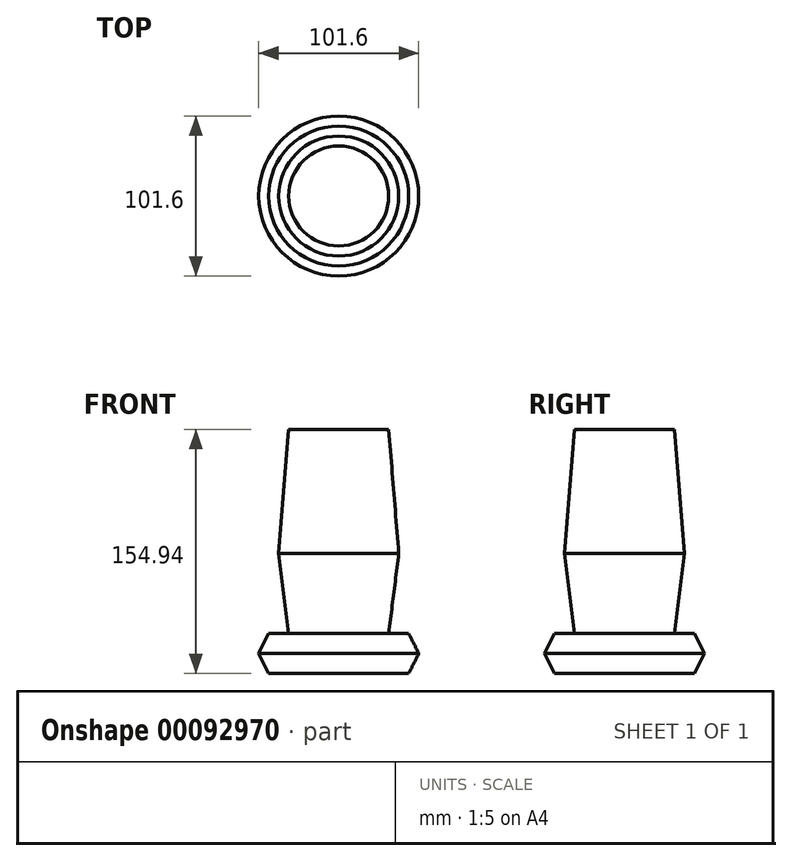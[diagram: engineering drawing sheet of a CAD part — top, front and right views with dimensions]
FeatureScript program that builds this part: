
annotation { "Feature Type Name" : "Feature", "Feature Type Description" : "" }
export const myFeature = defineFeature(function(context is Context, id is Id, definition is map)
    precondition{}
    {
        {
            var Q0;
            Q0=qCreatedBy(makeId("Top.planeOp"),FACE);
            var sketch = newSketch(context, id + "F0", { "sketchPlane" : qUnion([Q0])});
            skCircle(sketch, "E0", {"center": v(0, 0) * mm, "radius": 44.45 * mm});
            skSolve(sketch);
        }
        {
            var Q0;
            Q0=qCreatedBy(makeId("Top.planeOp"),FACE);
            cPlane(context, id + "F1", {"entities" : qUnion([Q0]), "cplaneType" : CPlaneType.OFFSET, "offset" : 12.7 * mm, "width" : 152.4 * mm, "height" : 152.4 * mm});
        }
        {
            var Q0;
            Q0=qCreatedBy(id+"F1.planeOp",FACE);
            var sketch = newSketch(context, id + "F2", { "sketchPlane" : qUnion([Q0])});
            skCircle(sketch, "E1", {"center": v(0, 0) * mm, "radius": 50.8 * mm});
            skSolve(sketch);
        }
        {
            var Q0;
            Q0=makeQuery(id+"F0.imprint","IMPRINT",FACE,{"disambiguationData":[TD([[makeQuery(id+"F0.imprint","IMPRINT",EDGE,{"derivedFrom":sQuery(id+"F0.wireOp",EDGE,"E0")}),1.0]])]});
            var Q1;
            Q1=makeQuery(id+"F2.imprint","IMPRINT",FACE,{"disambiguationData":[TD([[makeQuery(id+"F2.imprint","IMPRINT",EDGE,{"derivedFrom":sQuery(id+"F2.wireOp",EDGE,"E1")}),1.0]])]});
            loft(context, id + "F3", {"sheetProfilesArray" : [{ "sheetProfileEntities" : qUnion([Q0]) }, { "sheetProfileEntities" : qUnion([Q1]) }]});
        }
        {
            var Q0;
            Q0=qCreatedBy(id+"F1.planeOp",FACE);
            cPlane(context, id + "F4", {"entities" : qUnion([Q0]), "cplaneType" : CPlaneType.OFFSET, "offset" : 12.7 * mm, "width" : 152.4 * mm, "height" : 152.4 * mm});
        }
        {
            var Q0;
            Q0=qCreatedBy(id+"F4.planeOp",FACE);
            var sketch = newSketch(context, id + "F5", { "sketchPlane" : qUnion([Q0])});
            skCircle(sketch, "E2", {"center": v(0, 0) * mm, "radius": 44.45 * mm});
            skSolve(sketch);
        }
        {
            var Q1;
            Q1=makeQuery(id+"F3.opLoft","CAP_FACE",FACE,{"disambiguationData":[OSD([makeQuery(id+"F2.imprint","IMPRINT",FACE,{"disambiguationData":[TD([[makeQuery(id+"F2.imprint","IMPRINT",EDGE,{"derivedFrom":sQuery(id+"F2.wireOp",EDGE,"E1")}),1.0]])]})])],"isStart":true});
            var Q2;
            Q2=makeQuery(id+"F5.imprint","IMPRINT",FACE,{"disambiguationData":[TD([[makeQuery(id+"F5.imprint","IMPRINT",EDGE,{"derivedFrom":sQuery(id+"F5.wireOp",EDGE,"E2")}),1.0]])]});
            loft(context, id + "F6", {"operationType" : NewBodyOperationType.ADD, "sheetProfilesArray" : [{ "sheetProfileEntities" : qUnion([Q1]) }, { "sheetProfileEntities" : qUnion([Q2]) }]});
        }
        {
            var Q0;
            Q0=qCreatedBy(id+"F4.planeOp",FACE);
            var sketch = newSketch(context, id + "F7", { "sketchPlane" : qUnion([Q0])});
            skCircle(sketch, "E3", {"center": v(0, 0) * mm, "radius": 31.75 * mm});
            skSolve(sketch);
        }
        {
            var Q0;
            Q0=qCreatedBy(id+"F4.planeOp",FACE);
            cPlane(context, id + "F8", {"entities" : qUnion([Q0]), "cplaneType" : CPlaneType.OFFSET, "offset" : 50.8 * mm, "width" : 152.4 * mm, "height" : 152.4 * mm});
        }
        {
            var Q0;
            Q0=qCreatedBy(id+"F8.planeOp",FACE);
            var sketch = newSketch(context, id + "F9", { "sketchPlane" : qUnion([Q0])});
            skCircle(sketch, "E4", {"center": v(0, 0) * mm, "radius": 38.1 * mm});
            skSolve(sketch);
        }
        {
            var Q1;
            Q1=makeQuery(id+"F7.imprint","IMPRINT",FACE,{"disambiguationData":[TD([[makeQuery(id+"F7.imprint","IMPRINT",EDGE,{"derivedFrom":sQuery(id+"F7.wireOp",EDGE,"E3")}),1.0]])]});
            var Q2;
            Q2=makeQuery(id+"F9.imprint","IMPRINT",FACE,{"disambiguationData":[TD([[makeQuery(id+"F9.imprint","IMPRINT",EDGE,{"derivedFrom":sQuery(id+"F9.wireOp",EDGE,"E4")}),1.0]])]});
            loft(context, id + "F10", {"operationType" : NewBodyOperationType.ADD, "sheetProfilesArray" : [{ "sheetProfileEntities" : qUnion([Q1]) }, { "sheetProfileEntities" : qUnion([Q2]) }]});
        }
        {
            var Q0;
            Q0=qCreatedBy(id+"F8.planeOp",FACE);
            cPlane(context, id + "F11", {"entities" : qUnion([Q0]), "cplaneType" : CPlaneType.OFFSET, "offset" : 78.74 * mm, "width" : 152.4 * mm, "height" : 152.4 * mm});
        }
        {
            var Q0;
            Q0=qCreatedBy(id+"F11.planeOp",FACE);
            var sketch = newSketch(context, id + "F12", { "sketchPlane" : qUnion([Q0])});
            skCircle(sketch, "E5", {"center": v(0, 0) * mm, "radius": 31.75 * mm});
            skSolve(sketch);
        }
        {
            var Q1;
            Q1=makeQuery(id+"F10.opLoft","CAP_FACE",FACE,{"disambiguationData":[OSD([makeQuery(id+"F9.imprint","IMPRINT",FACE,{"disambiguationData":[TD([[makeQuery(id+"F9.imprint","IMPRINT",EDGE,{"derivedFrom":sQuery(id+"F9.wireOp",EDGE,"E4")}),1.0]])]})])],"isStart":true});
            var Q2;
            Q2=makeQuery(id+"F12.imprint","IMPRINT",FACE,{"disambiguationData":[TD([[makeQuery(id+"F12.imprint","IMPRINT",EDGE,{"derivedFrom":sQuery(id+"F12.wireOp",EDGE,"E5")}),1.0]])]});
            loft(context, id + "F13", {"operationType" : NewBodyOperationType.ADD, "sheetProfilesArray" : [{ "sheetProfileEntities" : qUnion([Q1]) }, { "sheetProfileEntities" : qUnion([Q2]) }]});
        }
    });
